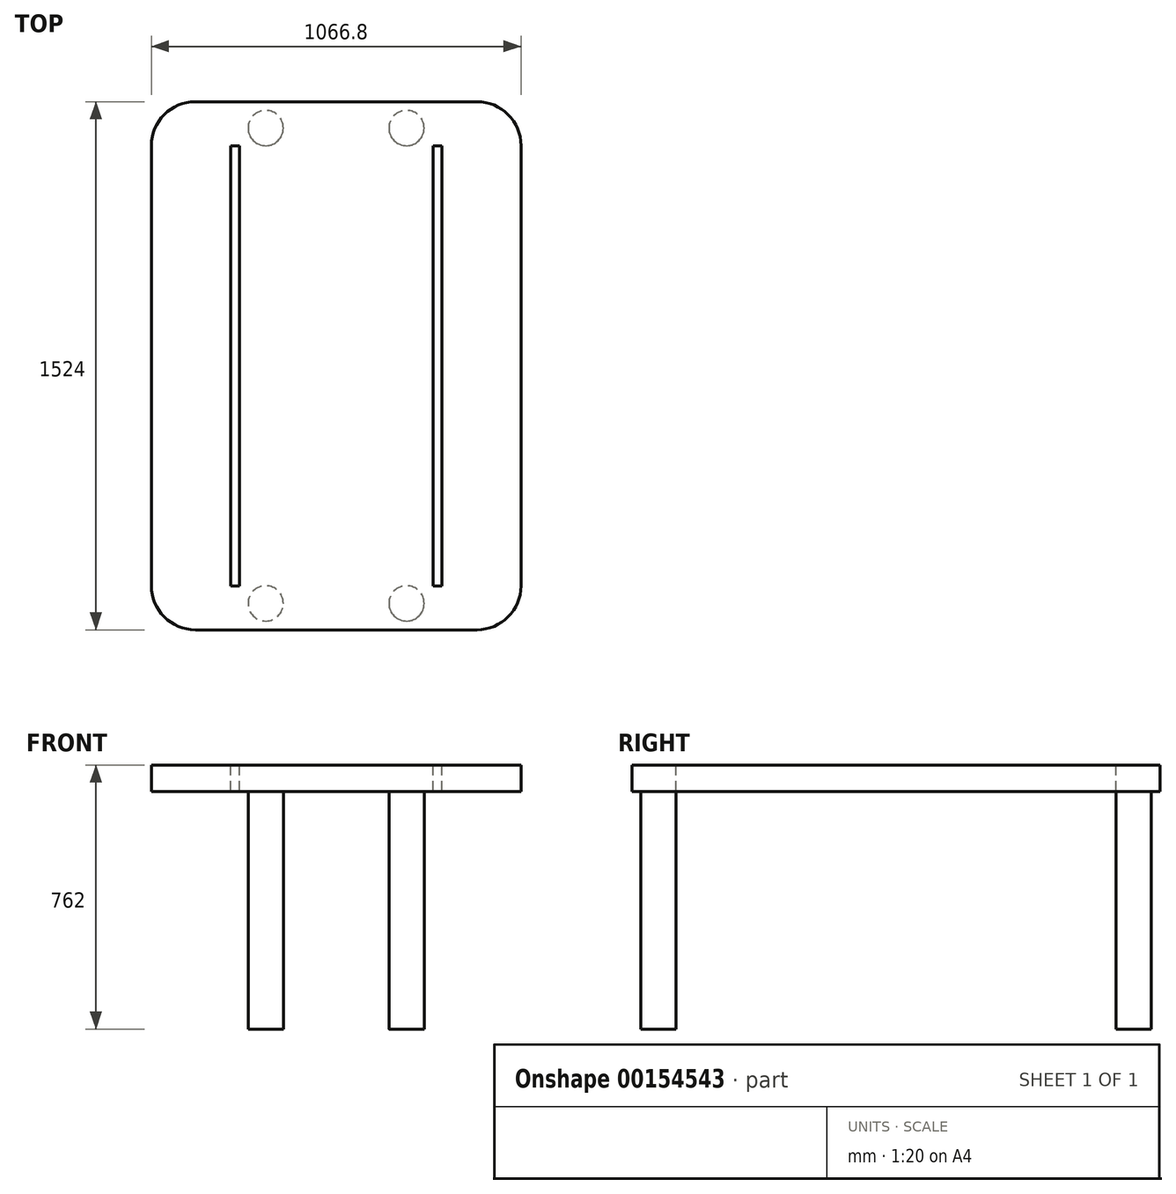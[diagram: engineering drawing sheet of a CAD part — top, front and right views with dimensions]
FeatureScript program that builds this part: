
annotation { "Feature Type Name" : "Feature", "Feature Type Description" : "" }
export const myFeature = defineFeature(function(context is Context, id is Id, definition is map)
    precondition{}
    {
        {
            var Q0;
            Q0=qCreatedBy(makeId("Top.planeOp"),FACE);
            var sketch = newSketch(context, id + "F0", { "sketchPlane" : qUnion([Q0])});
            skLineSegment(sketch, "E0.bottom", {"start": v(279.4, 762) * mm, "end": v(-279.4, 762) * mm});
            skLineSegment(sketch, "E0.top", {"start": v(279.4, -762) * mm, "end": v(-279.4, -762) * mm});
            skLineSegment(sketch, "E0.left", {"start": v(279.4, 762) * mm, "end": v(279.4, -762) * mm});
            skLineSegment(sketch, "E0.right", {"start": v(-279.4, 762) * mm, "end": v(-279.4, -762) * mm});
            skPoint(sketch, "E0.middle", {"position": v(0, 0) * mm});
            skSolve(sketch);
        }
        {
            var Q0;
            Q0=makeQuery(id+"F0.imprint","IMPRINT",FACE,{"disambiguationData":[TD([[makeQuery(id+"F0.imprint","IMPRINT",EDGE,{"derivedFrom":sQuery(id+"F0.wireOp",EDGE,"E0.bottom")}),1.0]])]});
            extrude(context, id + "F1", {"entities" : qUnion([Q0]), "depth" : 76.2 * mm});
        }
        {
            var Q0;
            Q0=makeQuery(id+"F1.opExtrude","CAP_FACE",FACE,{"disambiguationData":[OSD([sQuery(id+"F0.wireOp",EDGE,"E0.bottom"),sQuery(id+"F0.wireOp",EDGE,"E0.top"),sQuery(id+"F0.wireOp",EDGE,"E0.left"),sQuery(id+"F0.wireOp",EDGE,"E0.right")])],"isStart":true});
            var sketch = newSketch(context, id + "F2", { "sketchPlane" : qUnion([Q0])});
            skCircle(sketch, "E1", {"center": v(-203.2, 685.8) * mm, "radius": 50.8 * mm});
            skCircle(sketch, "E2", {"center": v(203.23, 685.8) * mm, "radius": 50.8 * mm});
            skCircle(sketch, "E3", {"center": v(203.2, -685.8) * mm, "radius": 50.8 * mm});
            skCircle(sketch, "E4", {"center": v(-203.2, -685.8) * mm, "radius": 50.8 * mm});
            skLineSegment(sketch, "E5", {"start": v(-203.2, 762) * mm, "end": v(-203.2, 685.8) * mm, "construction": true});
            skLineSegment(sketch, "E6", {"start": v(-203.2, 685.8) * mm, "end": v(-279.4, 685.8) * mm, "construction": true});
            skLineSegment(sketch, "E7", {"start": v(203.23, 762) * mm, "end": v(203.23, 685.8) * mm, "construction": true});
            skLineSegment(sketch, "E8", {"start": v(203.23, 685.8) * mm, "end": v(279.4, 687.97) * mm, "construction": true});
            skLineSegment(sketch, "E9", {"start": v(279.4, -685.8) * mm, "end": v(203.2, -685.8) * mm, "construction": true});
            skLineSegment(sketch, "E10", {"start": v(203.2, -762) * mm, "end": v(203.2, -685.8) * mm, "construction": true});
            skLineSegment(sketch, "E11", {"start": v(-203.2, -685.8) * mm, "end": v(-279.4, -685.8) * mm, "construction": true});
            skLineSegment(sketch, "E12", {"start": v(-203.2, -685.8) * mm, "end": v(-203.2, -762) * mm, "construction": true});
            skSolve(sketch);
        }
        {
            var Q0;
            Q0=makeQuery(id+"F2.imprint","IMPRINT",FACE,{"disambiguationData":[TD([[makeQuery(id+"F2.imprint","IMPRINT",EDGE,{"derivedFrom":sQuery(id+"F2.wireOp",EDGE,"E4")}),1.0]])]});
            var Q1;
            Q1=makeQuery(id+"F2.imprint","IMPRINT",FACE,{"disambiguationData":[TD([[makeQuery(id+"F2.imprint","IMPRINT",EDGE,{"derivedFrom":sQuery(id+"F2.wireOp",EDGE,"E3")}),1.0]])]});
            var Q2;
            Q2=makeQuery(id+"F2.imprint","IMPRINT",FACE,{"disambiguationData":[TD([[makeQuery(id+"F2.imprint","IMPRINT",EDGE,{"derivedFrom":sQuery(id+"F2.wireOp",EDGE,"E2")}),1.0]])]});
            var Q3;
            Q3=makeQuery(id+"F2.imprint","IMPRINT",FACE,{"disambiguationData":[TD([[makeQuery(id+"F2.imprint","IMPRINT",EDGE,{"derivedFrom":sQuery(id+"F2.wireOp",EDGE,"E1")}),1.0]])]});
            extrude(context, id + "F3", {"entities" : qUnion([Q0, Q1, Q2, Q3]), "operationType" : NewBodyOperationType.ADD, "depth" : 685.8 * mm});
        }
        {
            var Q0;
            Q0=makeQuery(id+"F1.opExtrude","CAP_FACE",FACE,{"disambiguationData":[OSD([sQuery(id+"F0.wireOp",EDGE,"E0.bottom"),sQuery(id+"F0.wireOp",EDGE,"E0.top"),sQuery(id+"F0.wireOp",EDGE,"E0.left"),sQuery(id+"F0.wireOp",EDGE,"E0.right")])],"isStart":false});
            var sketch = newSketch(context, id + "F4", { "sketchPlane" : qUnion([Q0])});
            skLineSegment(sketch, "E13.bottom", {"start": v(-279.4, 762) * mm, "end": v(-533.4, 762) * mm});
            skLineSegment(sketch, "E13.top", {"start": v(-279.4, -762) * mm, "end": v(-533.4, -762) * mm});
            skLineSegment(sketch, "E13.left", {"start": v(-279.4, 762) * mm, "end": v(-279.4, -762) * mm});
            skLineSegment(sketch, "E13.right", {"start": v(-533.4, 762) * mm, "end": v(-533.4, -762) * mm});
            skLineSegment(sketch, "E14.bottom", {"start": v(279.4, 762) * mm, "end": v(533.4, 762) * mm});
            skLineSegment(sketch, "E14.top", {"start": v(279.4, -762) * mm, "end": v(533.4, -762) * mm});
            skLineSegment(sketch, "E14.left", {"start": v(279.4, 762) * mm, "end": v(279.4, -762) * mm});
            skLineSegment(sketch, "E14.right", {"start": v(533.4, 762) * mm, "end": v(533.4, -762) * mm});
            skLineSegment(sketch, "E15.bottom", {"start": v(-279.4, 635) * mm, "end": v(-304.8, 635) * mm});
            skLineSegment(sketch, "E15.top", {"start": v(-279.4, -635) * mm, "end": v(-304.8, -635) * mm});
            skLineSegment(sketch, "E15.left", {"start": v(-279.4, 635) * mm, "end": v(-279.4, -635) * mm});
            skLineSegment(sketch, "E15.right", {"start": v(-304.8, 635) * mm, "end": v(-304.8, -635) * mm});
            skLineSegment(sketch, "E16.bottom", {"start": v(279.4, 635) * mm, "end": v(304.8, 635) * mm});
            skLineSegment(sketch, "E16.top", {"start": v(279.4, -635) * mm, "end": v(304.8, -635) * mm});
            skLineSegment(sketch, "E16.left", {"start": v(279.4, 635) * mm, "end": v(279.4, -635) * mm});
            skLineSegment(sketch, "E16.right", {"start": v(304.8, 635) * mm, "end": v(304.8, -635) * mm});
            skSolve(sketch);
        }
        {
            var Q0;
            {var subQ4=sQuery(id+"F4.wireOp",EDGE,"E13.bottom");Q0=makeQuery(id+"F4.imprint","IMPRINT",FACE,{"disambiguationData":[TD([[makeQuery(id+"F4.imprint","IMPRINT",EDGE,{"derivedFrom":subQ4}),1.0]])]});}
            var Q1;
            {var subQ4=sQuery(id+"F4.wireOp",EDGE,"E14.bottom");Q1=makeQuery(id+"F4.imprint","IMPRINT",FACE,{"disambiguationData":[TD([[makeQuery(id+"F4.imprint","IMPRINT",EDGE,{"derivedFrom":subQ4}),-1.0]])]});}
            extrude(context, id + "F5", {"entities" : qUnion([Q0, Q1]), "operationType" : NewBodyOperationType.ADD, "oppositeDirection" : true, "depth" : 76.2 * mm});
        }
        {
            var Q0;
            Q0=makeQuery(id+"F5.opExtrude","SWEPT_EDGE",EDGE,{"disambiguationData":[OSD([sQuery(id+"F4.wireOp",EDGE,"E13.top"),sQuery(id+"F4.wireOp",EDGE,"E13.right")])]});
            var Q1;
            Q1=makeQuery(id+"F5.opExtrude","SWEPT_EDGE",EDGE,{"disambiguationData":[OSD([sQuery(id+"F4.wireOp",EDGE,"E14.top"),sQuery(id+"F4.wireOp",EDGE,"E14.right")])]});
            var Q2;
            Q2=makeQuery(id+"F5.opExtrude","SWEPT_EDGE",EDGE,{"disambiguationData":[OSD([sQuery(id+"F4.wireOp",EDGE,"E14.bottom"),sQuery(id+"F4.wireOp",EDGE,"E14.right")])]});
            var Q3;
            Q3=makeQuery(id+"F5.opExtrude","SWEPT_EDGE",EDGE,{"disambiguationData":[OSD([sQuery(id+"F4.wireOp",EDGE,"E13.bottom"),sQuery(id+"F4.wireOp",EDGE,"E13.right")])]});
            fillet(context, id + "F6", {"entities" : qUnion([Q0, Q1, Q2, Q3]), "radius" : 127 * mm, "tangentPropagation" : true, "allowEdgeOverflow" : false});
        }
    });
